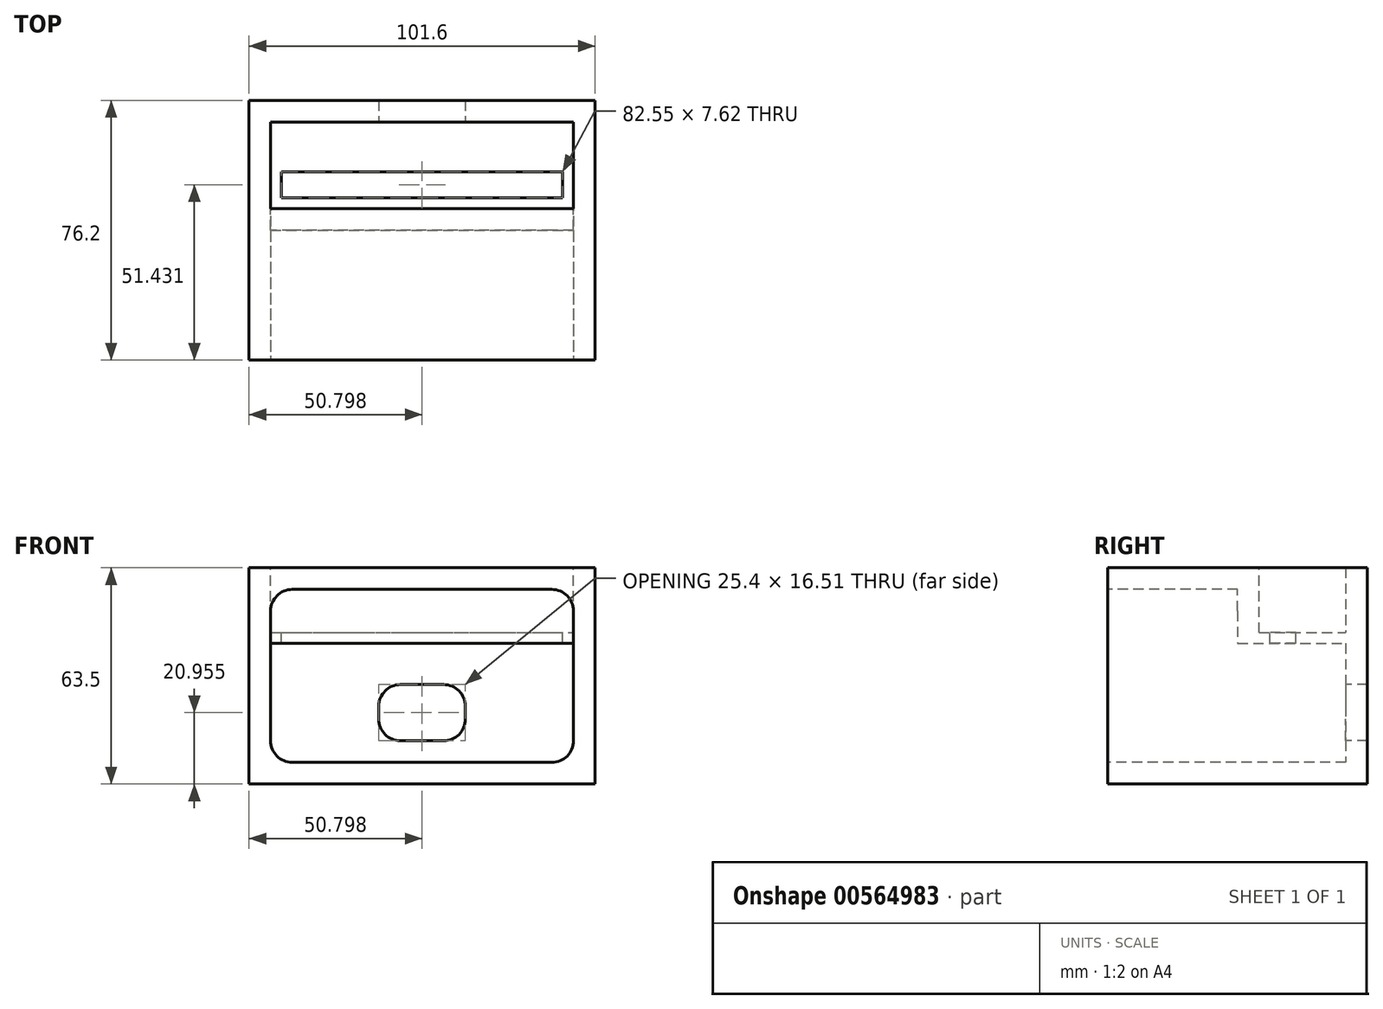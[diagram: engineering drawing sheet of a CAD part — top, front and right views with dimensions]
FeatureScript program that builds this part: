
annotation { "Feature Type Name" : "Feature", "Feature Type Description" : "" }
export const myFeature = defineFeature(function(context is Context, id is Id, definition is map)
    precondition{}
    {
        {
            var Q0;
            Q0=qCreatedBy(makeId("Top.planeOp"),FACE);
            var sketch = newSketch(context, id + "F0", { "sketchPlane" : qUnion([Q0])});
            skLineSegment(sketch, "E0.bottom", {"start": v(-100.44, 31.9) * mm, "end": v(1.16, 31.9) * mm});
            skLineSegment(sketch, "E0.top", {"start": v(-100.44, -44.3) * mm, "end": v(1.16, -44.3) * mm});
            skLineSegment(sketch, "E0.left", {"start": v(-100.44, 31.9) * mm, "end": v(-100.44, -44.3) * mm});
            skLineSegment(sketch, "E0.right", {"start": v(1.16, 31.9) * mm, "end": v(1.16, -44.3) * mm});
            skSolve(sketch);
        }
        {
            var Q0;
            Q0=makeQuery(id+"F0.imprint","IMPRINT",FACE,{"disambiguationData":[TD([[makeQuery(id+"F0.imprint","IMPRINT",EDGE,{"derivedFrom":sQuery(id+"F0.wireOp",EDGE,"E0.bottom")}),-1.0]])]});
            extrude(context, id + "F1", {"entities" : qUnion([Q0]), "depth" : 63.5 * mm, "offsetDistance" : 25.4 * mm});
        }
        {
            var Q0;
            Q0=makeQuery(id+"F1.opExtrude","SWEPT_FACE",FACE,{"disambiguationData":[OSD([sQuery(id+"F0.wireOp",EDGE,"E0.top")])]});
            var sketch = newSketch(context, id + "F2", { "sketchPlane" : qUnion([Q0])});
            skLineSegment(sketch, "E1.bottom", {"start": v(-87.74, 57.15) * mm, "end": v(-11.54, 57.15) * mm});
            skLineSegment(sketch, "E1.top", {"start": v(-87.74, 6.35) * mm, "end": v(-11.54, 6.35) * mm});
            skLineSegment(sketch, "E1.left", {"start": v(-94.1, 50.8) * mm, "end": v(-94.1, 12.7) * mm});
            skLineSegment(sketch, "E1.right", {"start": v(-5.2, 50.8) * mm, "end": v(-5.2, 12.7) * mm});
            skPoint(sketch, "E2.visualSharp", {"position": v(-94.1, 57.15) * mm});
            skArc(sketch, "E2.filletArc", {"start": v(-87.74, 57.15) * mm, "mid": v(-92.23, 55.3) * mm, "end": v(-94.1, 50.8) * mm});
            skPoint(sketch, "E3.visualSharp", {"position": v(-94.1, 6.35) * mm});
            skArc(sketch, "E3.filletArc", {"start": v(-94.1, 12.7) * mm, "mid": v(-92.23, 8.2) * mm, "end": v(-87.74, 6.35) * mm});
            skPoint(sketch, "E4.visualSharp", {"position": v(-5.2, 6.35) * mm});
            skArc(sketch, "E4.filletArc", {"start": v(-11.54, 6.35) * mm, "mid": v(-7.05, 8.2) * mm, "end": v(-5.2, 12.7) * mm});
            skPoint(sketch, "E5.visualSharp", {"position": v(-5.2, 57.15) * mm});
            skArc(sketch, "E5.filletArc", {"start": v(-5.2, 50.8) * mm, "mid": v(-7.05, 55.3) * mm, "end": v(-11.54, 57.15) * mm});
            skSolve(sketch);
        }
        {
            var Q0;
            Q0 = qSketchRegion(id + "F2", true);
            extrude(context, id + "F3", {"entities" : qUnion([Q0]), "operationType" : NewBodyOperationType.REMOVE, "oppositeDirection" : true, "depth" : 69.85 * mm, "offsetDistance" : 25.4 * mm});
        }
        {
            var Q0;
            Q0=makeQuery(id+"F1.opExtrude","CAP_FACE",FACE,{"disambiguationData":[OSD([sQuery(id+"F0.wireOp",EDGE,"E0.bottom"),sQuery(id+"F0.wireOp",EDGE,"E0.top"),sQuery(id+"F0.wireOp",EDGE,"E0.left"),sQuery(id+"F0.wireOp",EDGE,"E0.right")])],"isStart":false});
            var sketch = newSketch(context, id + "F4", { "sketchPlane" : qUnion([Q0])});
            skLineSegment(sketch, "E6.bottom", {"start": v(-94.1, 25.56) * mm, "end": v(-5.2, 25.56) * mm});
            skLineSegment(sketch, "E6.top", {"start": v(-94.1, 0.16) * mm, "end": v(-5.2, 0.16) * mm});
            skLineSegment(sketch, "E6.left", {"start": v(-94.1, 25.56) * mm, "end": v(-94.1, 0.16) * mm});
            skLineSegment(sketch, "E6.right", {"start": v(-5.2, 25.56) * mm, "end": v(-5.2, 0.16) * mm});
            skSolve(sketch);
        }
        {
            var Q0;
            Q0 = qSketchRegion(id + "F4", true);
            extrude(context, id + "F5", {"entities" : qUnion([Q0]), "operationType" : NewBodyOperationType.REMOVE, "oppositeDirection" : true, "depth" : 25.4 * mm, "offsetDistance" : 25.4 * mm});
        }
        {
            var Q0;
            Q0=makeQuery(id+"F5.boolean.opBoolean","MERGE",FACE,{"derivedFrom":[makeQuery(id+"F3.boolean.opBoolean","COPY",FACE,{"derivedFrom":makeQuery(id+"F3.opExtrude","CAP_FACE",FACE,{"disambiguationData":[OSD([sQuery(id+"F2.wireOp",EDGE,"E1.bottom"),sQuery(id+"F2.wireOp",EDGE,"E1.top"),sQuery(id+"F2.wireOp",EDGE,"E1.left"),sQuery(id+"F2.wireOp",EDGE,"E1.right"),sQuery(id+"F2.wireOp",EDGE,"E2.filletArc"),sQuery(id+"F2.wireOp",EDGE,"E3.filletArc"),sQuery(id+"F2.wireOp",EDGE,"E4.filletArc"),sQuery(id+"F2.wireOp",EDGE,"E5.filletArc")])],"isStart":false})}),makeQuery(id+"F5.opExtrude","SWEPT_FACE",FACE,{"disambiguationData":[OSD([sQuery(id+"F4.wireOp",EDGE,"E6.bottom")])]})]});
            var sketch = newSketch(context, id + "F6", { "sketchPlane" : qUnion([Q0])});
            skLineSegment(sketch, "E7.bottom", {"start": v(-56, 29.2) * mm, "end": v(-43.3, 29.2) * mm});
            skLineSegment(sketch, "E7.top", {"start": v(-56, 12.7) * mm, "end": v(-43.3, 12.7) * mm});
            skLineSegment(sketch, "E7.left", {"start": v(-62.34, 22.86) * mm, "end": v(-62.34, 19.05) * mm});
            skLineSegment(sketch, "E7.right", {"start": v(-36.94, 22.86) * mm, "end": v(-36.94, 19.05) * mm});
            skPoint(sketch, "E8.visualSharp", {"position": v(-62.34, 29.2) * mm});
            skArc(sketch, "E8.filletArc", {"start": v(-56, 29.2) * mm, "mid": v(-60.48, 27.35) * mm, "end": v(-62.34, 22.86) * mm});
            skPoint(sketch, "E9.visualSharp", {"position": v(-62.34, 12.7) * mm});
            skArc(sketch, "E9.filletArc", {"start": v(-62.34, 19.05) * mm, "mid": v(-60.48, 14.56) * mm, "end": v(-56, 12.7) * mm});
            skPoint(sketch, "E10.visualSharp", {"position": v(-36.94, 29.2) * mm});
            skArc(sketch, "E10.filletArc", {"start": v(-36.94, 22.86) * mm, "mid": v(-38.8, 27.35) * mm, "end": v(-43.3, 29.2) * mm});
            skPoint(sketch, "E11.visualSharp", {"position": v(-36.94, 12.7) * mm});
            skArc(sketch, "E11.filletArc", {"start": v(-43.3, 12.7) * mm, "mid": v(-38.8, 14.56) * mm, "end": v(-36.94, 19.05) * mm});
            skSolve(sketch);
        }
        {
            var Q0;
            Q0=makeQuery(id+"F6.imprint","IMPRINT",FACE,{"disambiguationData":[TD([[makeQuery(id+"F6.imprint","IMPRINT",EDGE,{"derivedFrom":sQuery(id+"F6.wireOp",EDGE,"E7.bottom")}),-1.0]])]});
            extrude(context, id + "F7", {"entities" : qUnion([Q0]), "operationType" : NewBodyOperationType.REMOVE, "oppositeDirection" : true, "depth" : 25.4 * mm, "offsetDistance" : 25.4 * mm});
        }
        {
            var Q0;
            Q0=makeQuery(id+"F5.boolean.opBoolean","MERGE",FACE,{"derivedFrom":[makeQuery(id+"F3.boolean.opBoolean","COPY",FACE,{"derivedFrom":makeQuery(id+"F3.opExtrude","CAP_FACE",FACE,{"disambiguationData":[OSD([sQuery(id+"F2.wireOp",EDGE,"E1.bottom"),sQuery(id+"F2.wireOp",EDGE,"E1.top"),sQuery(id+"F2.wireOp",EDGE,"E1.left"),sQuery(id+"F2.wireOp",EDGE,"E1.right"),sQuery(id+"F2.wireOp",EDGE,"E2.filletArc"),sQuery(id+"F2.wireOp",EDGE,"E3.filletArc"),sQuery(id+"F2.wireOp",EDGE,"E4.filletArc"),sQuery(id+"F2.wireOp",EDGE,"E5.filletArc")])],"isStart":false})}),makeQuery(id+"F5.opExtrude","SWEPT_FACE",FACE,{"disambiguationData":[OSD([sQuery(id+"F4.wireOp",EDGE,"E6.bottom")])]})]});
            var sketch = newSketch(context, id + "F8", { "sketchPlane" : qUnion([Q0])});
            skLineSegment(sketch, "E12.bottom", {"start": v(-94.1, 41.28) * mm, "end": v(-5.2, 41.28) * mm});
            skLineSegment(sketch, "E12.top", {"start": v(-94.1, 44.45) * mm, "end": v(-5.2, 44.45) * mm});
            skLineSegment(sketch, "E12.left", {"start": v(-94.1, 41.28) * mm, "end": v(-94.1, 44.45) * mm});
            skLineSegment(sketch, "E12.right", {"start": v(-5.2, 41.28) * mm, "end": v(-5.2, 44.45) * mm});
            skSolve(sketch);
        }
        {
            var Q0;
            Q0 = qSketchRegion(id + "F8", true);
            extrude(context, id + "F9", {"entities" : qUnion([Q0]), "operationType" : NewBodyOperationType.ADD, "depth" : 31.75 * mm, "offsetDistance" : 25.4 * mm});
        }
        {
            var Q0;
            Q0=makeQuery(id+"F1.opExtrude","CAP_FACE",FACE,{"disambiguationData":[OSD([sQuery(id+"F0.wireOp",EDGE,"E0.bottom"),sQuery(id+"F0.wireOp",EDGE,"E0.top"),sQuery(id+"F0.wireOp",EDGE,"E0.left"),sQuery(id+"F0.wireOp",EDGE,"E0.right")])],"isStart":false});
            var sketch = newSketch(context, id + "F10", { "sketchPlane" : qUnion([Q0])});
            skPoint(sketch, "E13.oppositeSnap0", {"position": v(1.16, -6.2) * mm});
            skLineSegment(sketch, "E13.bottom", {"start": v(-94.1, 0.16) * mm, "end": v(-5.2, 0.16) * mm});
            skLineSegment(sketch, "E13.top", {"start": v(-94.1, -6.2) * mm, "end": v(-5.2, -6.2) * mm});
            skLineSegment(sketch, "E13.left", {"start": v(-94.1, 0.16) * mm, "end": v(-94.1, -6.2) * mm});
            skLineSegment(sketch, "E13.right", {"start": v(-5.2, 0.16) * mm, "end": v(-5.2, -6.2) * mm});
            skSolve(sketch);
        }
        {
            var Q0;
            Q0 = qSketchRegion(id + "F10", true);
            extrude(context, id + "F11", {"entities" : qUnion([Q0]), "operationType" : NewBodyOperationType.ADD, "oppositeDirection" : true, "depth" : 19.05 * mm, "offsetDistance" : 25.4 * mm});
        }
        {
            var Q0;
            Q0=makeQuery(id+"F9.opExtrude","SWEPT_FACE",FACE,{"disambiguationData":[OSD([sQuery(id+"F8.wireOp",EDGE,"E12.top")])]});
            var sketch = newSketch(context, id + "F12", { "sketchPlane" : qUnion([Q0])});
            skLineSegment(sketch, "E14.bottom", {"start": v(-90.92, 10.95) * mm, "end": v(-8.37, 10.95) * mm});
            skLineSegment(sketch, "E14.top", {"start": v(-90.92, 3.33) * mm, "end": v(-8.37, 3.33) * mm});
            skLineSegment(sketch, "E14.left", {"start": v(-90.92, 10.95) * mm, "end": v(-90.92, 3.33) * mm});
            skLineSegment(sketch, "E14.right", {"start": v(-8.37, 10.95) * mm, "end": v(-8.37, 3.33) * mm});
            skSolve(sketch);
        }
        {
            var Q0;
            Q0=makeQuery(id+"F12.imprint","IMPRINT",FACE,{"disambiguationData":[TD([[makeQuery(id+"F12.imprint","IMPRINT",EDGE,{"derivedFrom":sQuery(id+"F12.wireOp",EDGE,"E14.bottom")}),-1.0]])]});
            extrude(context, id + "F13", {"entities" : qUnion([Q0]), "operationType" : NewBodyOperationType.REMOVE, "oppositeDirection" : true, "depth" : 25.4 * mm, "offsetDistance" : 25.4 * mm});
        }
    });
